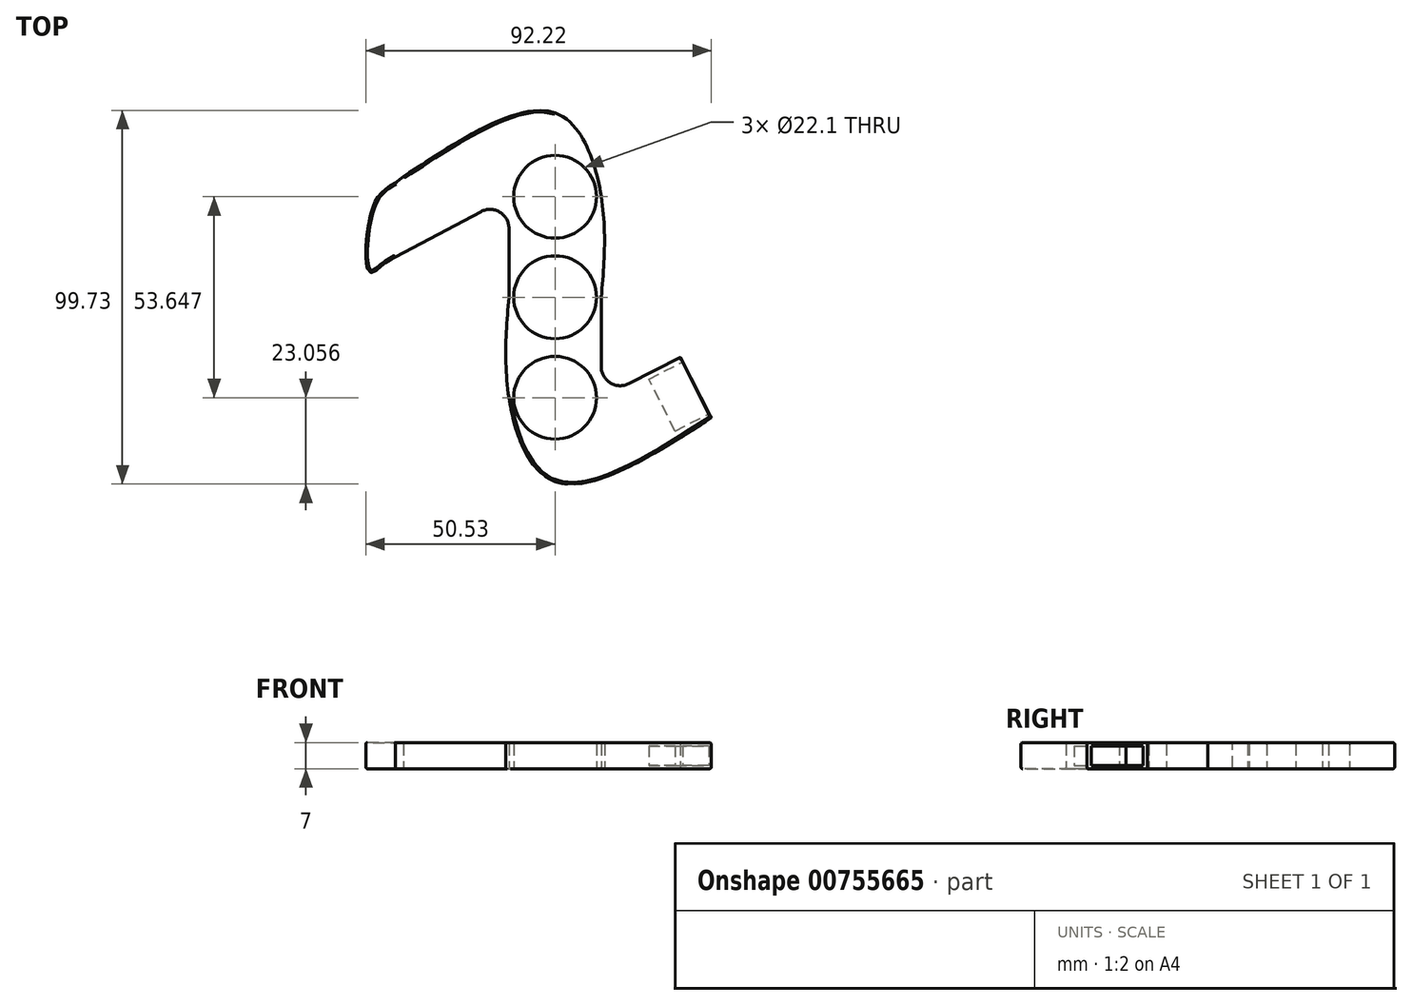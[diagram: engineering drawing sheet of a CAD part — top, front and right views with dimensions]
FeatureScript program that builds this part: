
annotation { "Feature Type Name" : "Feature", "Feature Type Description" : "" }
export const myFeature = defineFeature(function(context is Context, id is Id, definition is map)
    precondition{}
    {
        {
            var Q0;
            Q0=qCreatedBy(makeId("Top.planeOp"),FACE);
            var sketch = newSketch(context, id + "F0", { "sketchPlane" : qUnion([Q0])});
            skCircle(sketch, "E0", {"center": v(0, 0) * mm, "radius": 11.05 * mm});
            skCircle(sketch, "E1", {"center": v(0, -26.82) * mm, "radius": 11.05 * mm});
            skCircle(sketch, "E2.MirrorC", {"center": v(0, 26.82) * mm, "radius": 11.05 * mm});
            skLineSegment(sketch, "E3", {"start": v(11.05, 0) * mm, "end": v(12.32, 0) * mm, "construction": true});
            skLineSegment(sketch, "E4.MirrorCS", {"start": v(-11.05, 0) * mm, "end": v(-12.32, 0) * mm, "construction": true});
            skLineSegment(sketch, "E5", {"start": v(12.32, 26.82) * mm, "end": v(11.05, 26.82) * mm});
            skLineSegment(sketch, "E6", {"start": v(11.05, -26.82) * mm, "end": v(12.32, -26.82) * mm});
            skLineSegment(sketch, "E7.MirrorCS", {"start": v(-12.32, 26.82) * mm, "end": v(-11.05, 26.82) * mm});
            skLineSegment(sketch, "E8.MirrorCS", {"start": v(-11.05, -26.82) * mm, "end": v(-12.32, -26.82) * mm});
            skFitSpline(sketch, "E9", {"points": [v(-12.32, 0) * mm, v(-12.32, -26.82) * mm, v(0, -49.2) * mm, v(41.69, -32.23) * mm], "startDerivative": vector(-7.36, -84.39) * mm, "endDerivative": vector(121.47, 77.36) * mm});
            skLineSegment(sketch, "E10", {"start": v(0, 37.87) * mm, "end": v(0, 49.2) * mm});
            skLineSegment(sketch, "E11", {"start": v(-11.05, 26.82) * mm, "end": v(-11.05, 32.23) * mm});
            skLineSegment(sketch, "E12", {"start": v(-11.05, 32.23) * mm, "end": v(-40.41, 32.23) * mm});
            skFitSpline(sketch, "E13", {"points": [v(12.32, 0) * mm, v(12.32, 26.82) * mm, v(0, 49.2) * mm, v(-40.41, 32.23) * mm], "startDerivative": vector(7.4, 83.86) * mm, "endDerivative": vector(-118.35, -77.55) * mm});
            skLineSegment(sketch, "E14", {"start": v(-40.41, 32.23) * mm, "end": v(-40.41, 11.91) * mm, "construction": true});
            skLineSegment(sketch, "E15", {"start": v(33.49, -16.08) * mm, "end": v(12.32, -26.82) * mm});
            skLineSegment(sketch, "E16", {"start": v(12.32, 0) * mm, "end": v(12.32, -26.82) * mm});
            skLineSegment(sketch, "E17", {"start": v(-12.32, 0) * mm, "end": v(-12.32, 26.82) * mm});
            skLineSegment(sketch, "E18", {"start": v(-40.41, 11.91) * mm, "end": v(-12.32, 26.82) * mm});
            skLineSegment(sketch, "E19", {"start": v(-40.41, 32.23) * mm, "end": v(-42.67, 30.6) * mm});
            skLineSegment(sketch, "E20", {"start": v(-40.41, 11.91) * mm, "end": v(-42.67, 10.71) * mm});
            skFitSpline(sketch, "E21", {"points": [v(-42.67, 10.71) * mm, v(-46.18, 8.55) * mm, v(-49.5, 6.7) * mm, v(-48.58, 24.22) * mm, v(-42.67, 30.6) * mm], "startDerivative": vector(-18.54, -9.2) * mm, "endDerivative": vector(25.09, 14.2) * mm});
            skLineSegment(sketch, "E22", {"start": v(41.69, -32.23) * mm, "end": v(33.49, -16.08) * mm});
            skSolve(sketch);
        }
        {
            var Q0;
            Q0 = qSketchRegion(id + "F0", true);
            extrude(context, id + "F1", {"entities" : qUnion([Q0]), "depth" : 7 * mm, "offsetDistance" : 25.4 * mm});
        }
        {
            var Q0;
            Q0=makeQuery(id+"F1.opExtrude","SWEPT_EDGE",EDGE,{"disambiguationData":[OSD([sQuery(id+"F0.wireOp",EDGE,"E6"),sQuery(id+"F0.wireOp",EDGE,"E15"),sQuery(id+"F0.wireOp",EDGE,"E16")])]});
            fillet(context, id + "F2", {"entities" : qUnion([Q0]), "radius" : 5.08 * mm, "tangentPropagation" : true, "allowEdgeOverflow" : false});
        }
        {
            var Q0;
            Q0=makeQuery(id+"F1.opExtrude","SWEPT_EDGE",EDGE,{"disambiguationData":[OSD([sQuery(id+"F0.wireOp",EDGE,"E7.MirrorCS"),sQuery(id+"F0.wireOp",EDGE,"E17"),sQuery(id+"F0.wireOp",EDGE,"E18")])]});
            fillet(context, id + "F3", {"entities" : qUnion([Q0]), "radius" : 5.08 * mm, "tangentPropagation" : true, "allowEdgeOverflow" : false});
        }
        {
            var Q0;
            Q0=makeQuery(id+"F1.opExtrude","CAP_EDGE",EDGE,{"disambiguationData":[OSD([sQuery(id+"F0.wireOp",EDGE,"E2.MirrorC")])],"isStart":false});
            fillet(context, id + "F4", {"entities" : qUnion([Q0]), "radius" : 0.43 * mm, "tangentPropagation" : true, "allowEdgeOverflow" : false});
        }
        {
            var Q0;
            Q0=makeQuery(id+"F1.opExtrude","SWEPT_FACE",FACE,{"disambiguationData":[OSD([sQuery(id+"F0.wireOp",EDGE,"E0")])]});
            fillet(context, id + "F5", {"entities" : qUnion([Q0]), "radius" : 0.43 * mm, "tangentPropagation" : true, "allowEdgeOverflow" : false});
        }
        {
            var Q0;
            Q0=makeQuery(id+"F1.opExtrude","SWEPT_FACE",FACE,{"disambiguationData":[OSD([sQuery(id+"F0.wireOp",EDGE,"E2.MirrorC")])]});
            var Q1;
            Q1=makeQuery(id+"F1.opExtrude","SWEPT_FACE",FACE,{"disambiguationData":[OSD([sQuery(id+"F0.wireOp",EDGE,"E1")])]});
            fillet(context, id + "F6", {"entities" : qUnion([Q0, Q1]), "radius" : 0.43 * mm, "tangentPropagation" : true, "allowEdgeOverflow" : false});
        }
        {
            var Q0;
            Q0=makeQuery(id+"F1.opExtrude","CAP_FACE",FACE,{"disambiguationData":[OSD([sQuery(id+"F0.wireOp",EDGE,"E0"),sQuery(id+"F0.wireOp",EDGE,"E1"),sQuery(id+"F0.wireOp",EDGE,"E2.MirrorC"),sQuery(id+"F0.wireOp",EDGE,"E9"),sQuery(id+"F0.wireOp",EDGE,"E13"),sQuery(id+"F0.wireOp",EDGE,"SSbbWdvb-wKyO-htta-P4pP-IS62pagtKvRM"),sQuery(id+"F0.wireOp",EDGE,"E15"),sQuery(id+"F0.wireOp",EDGE,"E16"),sQuery(id+"F0.wireOp",EDGE,"E17"),sQuery(id+"F0.wireOp",EDGE,"E18"),sQuery(id+"F0.wireOp",EDGE,"E19"),sQuery(id+"F0.wireOp",EDGE,"E20"),sQuery(id+"F0.wireOp",EDGE,"E21")])],"isStart":false});
            fillet(context, id + "F7", {"entities" : qUnion([Q0]), "radius" : 0.43 * mm, "tangentPropagation" : true, "allowEdgeOverflow" : false});
        }
        {
            var Q0;
            Q0=makeQuery(id+"F1.opExtrude","CAP_FACE",FACE,{"disambiguationData":[OSD([sQuery(id+"F0.wireOp",EDGE,"E0"),sQuery(id+"F0.wireOp",EDGE,"E1"),sQuery(id+"F0.wireOp",EDGE,"E2.MirrorC"),sQuery(id+"F0.wireOp",EDGE,"E9"),sQuery(id+"F0.wireOp",EDGE,"E13"),sQuery(id+"F0.wireOp",EDGE,"SSbbWdvb-wKyO-htta-P4pP-IS62pagtKvRM"),sQuery(id+"F0.wireOp",EDGE,"E15"),sQuery(id+"F0.wireOp",EDGE,"E16"),sQuery(id+"F0.wireOp",EDGE,"E17"),sQuery(id+"F0.wireOp",EDGE,"E18"),sQuery(id+"F0.wireOp",EDGE,"E19"),sQuery(id+"F0.wireOp",EDGE,"E20"),sQuery(id+"F0.wireOp",EDGE,"E21")])],"isStart":true});
            fillet(context, id + "F8", {"entities" : qUnion([Q0]), "radius" : 0.43 * mm, "tangentPropagation" : true, "allowEdgeOverflow" : false});
        }
        {
            var Q0;
            Q0=makeQuery(id+"F1.opExtrude","SWEPT_FACE",FACE,{"disambiguationData":[OSD([sQuery(id+"F0.wireOp",EDGE,"E22")])]});
            var sketch = newSketch(context, id + "F9", { "sketchPlane" : qUnion([Q0])});
            skLineSegment(sketch, "E23.bottom", {"start": v(-46.35, 6.13) * mm, "end": v(-30.82, 6.13) * mm});
            skLineSegment(sketch, "E23.top", {"start": v(-46.35, 0.88) * mm, "end": v(-30.82, 0.88) * mm});
            skLineSegment(sketch, "E23.left", {"start": v(-46.35, 6.13) * mm, "end": v(-46.35, 0.88) * mm});
            skLineSegment(sketch, "E23.right", {"start": v(-30.82, 6.13) * mm, "end": v(-30.82, 0.88) * mm});
            skSolve(sketch);
        }
        {
            var Q0;
            Q0 = qSketchRegion(id + "F9", true);
            extrude(context, id + "F10", {"entities" : qUnion([Q0]), "operationType" : NewBodyOperationType.REMOVE, "oppositeDirection" : true, "depth" : 10.16 * mm, "offsetDistance" : 25.4 * mm});
        }
    });
